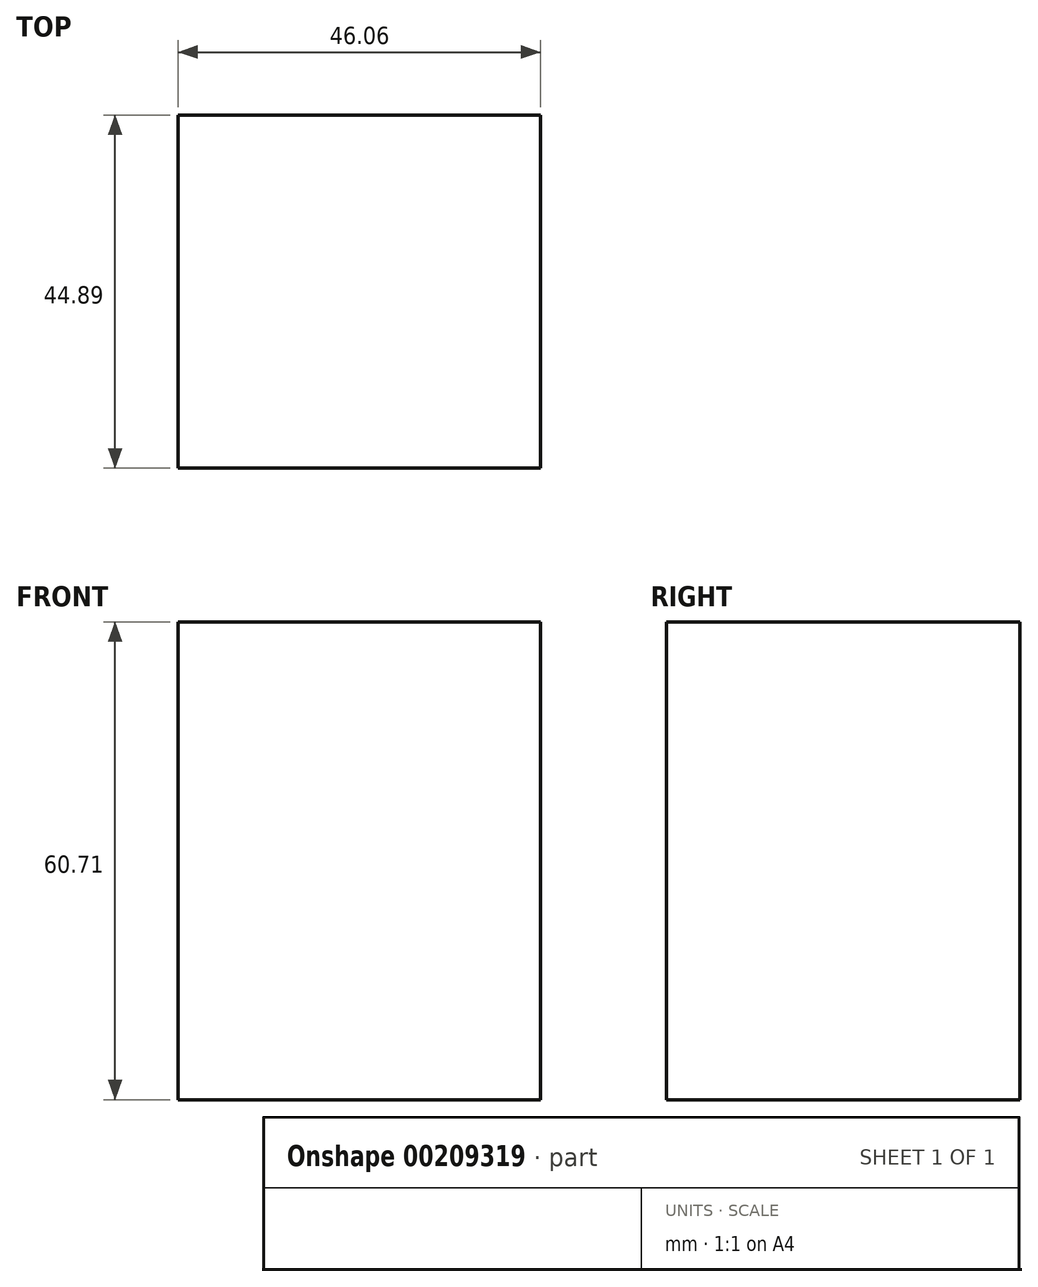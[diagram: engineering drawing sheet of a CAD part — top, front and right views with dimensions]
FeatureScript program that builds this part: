
annotation { "Feature Type Name" : "Feature", "Feature Type Description" : "" }
export const myFeature = defineFeature(function(context is Context, id is Id, definition is map)
    precondition{}
    {
        {
            var Q0;
            Q0=qCreatedBy(makeId("Top.planeOp"),FACE);
            var sketch = newSketch(context, id + "F0", { "sketchPlane" : qUnion([Q0])});
            skLineSegment(sketch, "E0.bottom", {"start": v(-22.74, 24.05) * mm, "end": v(23.32, 24.05) * mm});
            skLineSegment(sketch, "E0.top", {"start": v(-22.74, -20.84) * mm, "end": v(23.32, -20.84) * mm});
            skLineSegment(sketch, "E0.left", {"start": v(-22.74, 24.05) * mm, "end": v(-22.74, -20.84) * mm});
            skLineSegment(sketch, "E0.right", {"start": v(23.32, 24.05) * mm, "end": v(23.32, -20.84) * mm});
            skLineSegment(sketch, "E1.bottom", {"start": v(156.52, 0) * mm, "end": v(154.77, 0) * mm});
            skLineSegment(sketch, "E1.top", {"start": v(156.52, 0) * mm, "end": v(154.77, 0) * mm});
            skLineSegment(sketch, "E1.left", {"start": v(156.52, 0) * mm, "end": v(156.52, 0) * mm});
            skLineSegment(sketch, "E1.right", {"start": v(154.77, 0) * mm, "end": v(154.77, 0) * mm});
            skSolve(sketch);
        }
        {
            var Q0;
            Q0=makeQuery(id+"F0.imprint","IMPRINT",FACE,{"disambiguationData":[TD([[makeQuery(id+"F0.imprint","IMPRINT",EDGE,{"derivedFrom":sQuery(id+"F0.wireOp",EDGE,"E0.bottom")}),-1.0]])]});
            extrude(context, id + "F1", {"entities" : qUnion([Q0]), "depth" : 60.7 * mm});
        }
    });
